# Revit family: Hager-Univers-IP30-D160-QS-Cl.II-FWQ_encl-AT-de
name_source: partatom
category: Equipement électrique
units: mm (PartAtom-declared; Revit-internal decimal feet)

## family parameters
Configuration du panneau = Deux colonnes, circuits au sein
Cote de connecteur circulaire = Utiliser le diamètre
Couper avec des vides une fois chargée = Non
Hôte = Face
Partagée = Non
Point de calcul de pièce = Non
Type d'élément = Tableau de raccordement

## types (1)
- Aufputz IP30 B1050 H950 T160  - FWQ64D1
    Commentaires du type = Univers
    EF000003 - Montageart = EV000384 - Aufputz
    EF000007 - Farbe = EV000202 - weiß
    EF000008 - Breite = 1050 mm  [stored 3.44488 ft]
    EF000040 - Höhe = 950 mm  [stored 3.1168 ft]
    EF000049 - Tiefe = 160 mm  [stored 0.524934 ft]
    EF000116 - RAL-Nummer = 9010
    EF000118 - Mit Montageplatte = Oui
    EF000218 - Einbautiefe = 0 mm  [stored 0 ft]
    EF000266 - Anzahl der Reihen = 24
    EF000339 - Art der Abdeckung = EV001012 - Deckel
    EF000437 - Anzahl der Leitungseinführungen = 16
    EF001088 - Anbaumöglichkeit = Oui
    EF001131 - Innentiefe = 160 mm  [stored 0.524934 ft]
    EF001596 - Werkstoff des Gehäuses = EV000179 - Stahl
    EF001613 - Funktionserhalt = EV000494 - ohne
    EF002950 - Breite in Teilungseinheiten = 48
    EF003532 - Geeignet für Außengebrauch = Non
    EF004427 - Anzahl der Module = 288
    EF004464 - Art der Tür = EV002646 - Einzel
    EF005474 - Schutzart (IP) = EV006410 - IP30
    EF006244 - Transparenter Deckel/Tür = Non
    EF006306 - Mit Schloss = Non
    EF007800 - Geeignet für Blitzschutz = Non
    EF008873 - Nennstrom (In) = 125 A
    EF009170 - Materialstärke Gehäuse = 2 mm  [stored 0.00656168 ft]
    EF009171 - Materialstärke Tür/Deckel = 2 mm  [stored 0.00656168 ft]
    EF009212 - Ausführung Deckel = EV009916 - mit Ausschnitt
    EF009554 - Anzahl der Öffnungen für Flanschplatten = 8
    EF015940 - Deckel mit Überdruckentlastung = Non
    Elévation par défaut = 0 mm  [stored 0 ft]
    Fabricant = Hager
    HG000002 - Mit tür = Non
    HG000003 - Bereich = Univers
    HG000004 - Herstellerreferenz = FWQ64D1
    HG000006 - Unterputz = Non
    HG000009 - Doppelflügeligen Tür = Non
    HG000010 - Asymmetrische Türen = Non
    HG000023 - Gehäuse mit doppeltem Querschnitt = Non
    HG000024 - Höhe des unteren Teils = 800 mm  [stored 2.62467 ft]
    HG000026 - Stehend auf dem Boden = Non
    HG000027 - Sockelhöhe = 0 mm  [stored 0 ft]

note: [stored X ft] marks values corroborated as IEEE doubles in the binary element streams (Revit-internal decimal feet)

## geometry (parser evidence)
native form markers: Sweep x9
no freeform markers — native parametric forms only
